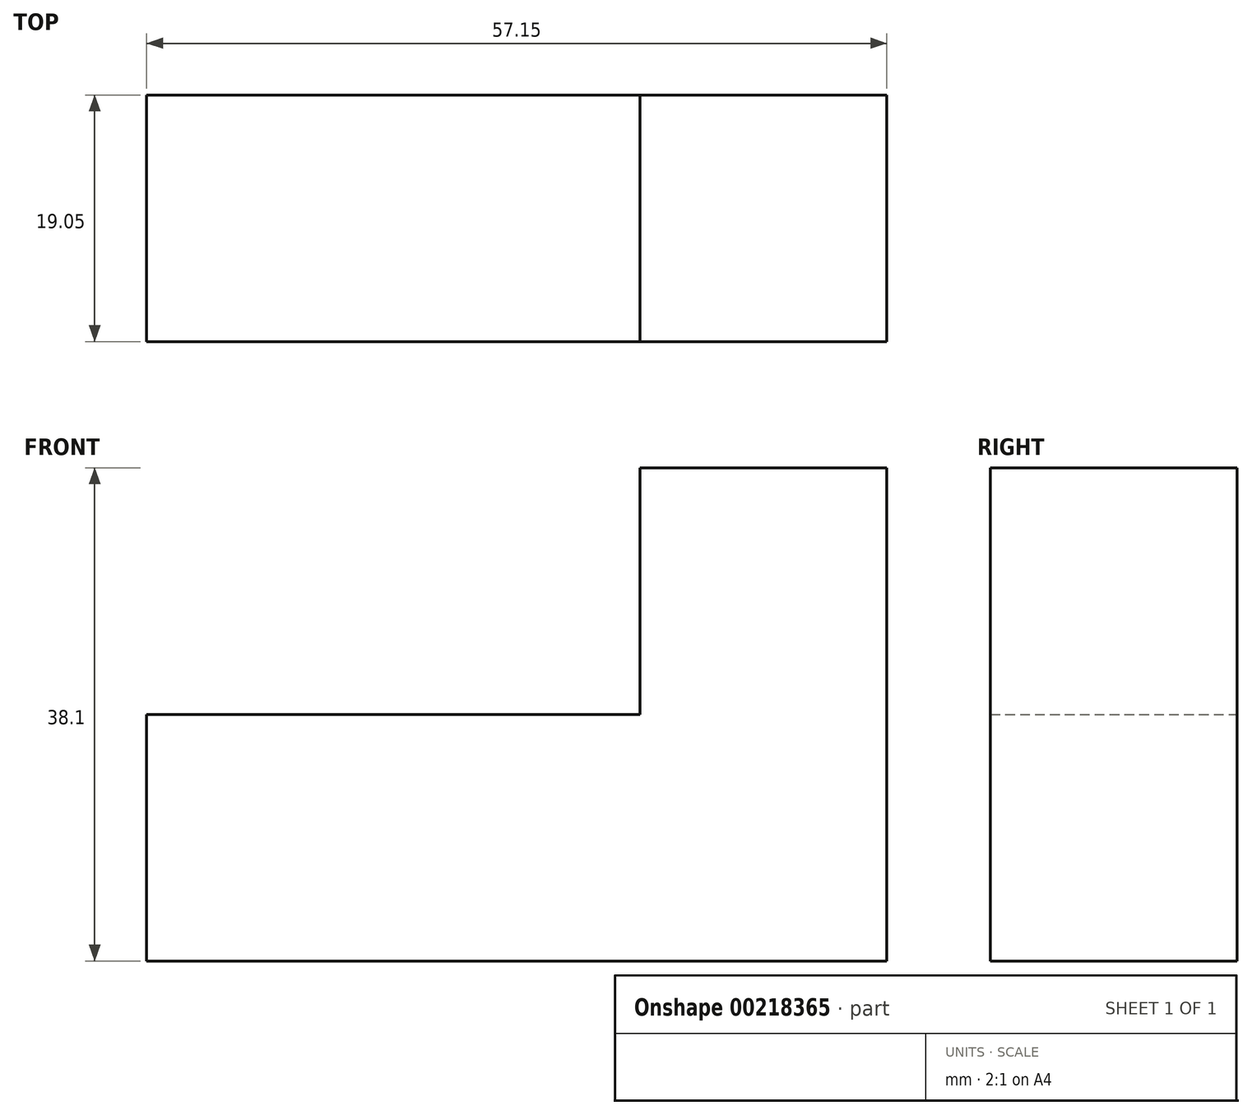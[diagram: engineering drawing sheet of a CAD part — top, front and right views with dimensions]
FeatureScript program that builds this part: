
annotation { "Feature Type Name" : "Feature", "Feature Type Description" : "" }
export const myFeature = defineFeature(function(context is Context, id is Id, definition is map)
    precondition{}
    {
        {
            var Q0;
            Q0=qCreatedBy(makeId("Front.planeOp"),FACE);
            var sketch = newSketch(context, id + "F0", { "sketchPlane" : qUnion([Q0])});
            skLineSegment(sketch, "E0.bottom", {"start": v(-57.15, 37.27) * mm, "end": v(-38.1, 37.27) * mm});
            skLineSegment(sketch, "E0.top", {"start": v(-57.15, 18.22) * mm, "end": v(-38.1, 18.22) * mm});
            skLineSegment(sketch, "E0.left", {"start": v(-57.15, 37.27) * mm, "end": v(-57.15, 18.22) * mm});
            skLineSegment(sketch, "E0.right", {"start": v(-38.1, 37.27) * mm, "end": v(-38.1, 18.22) * mm});
            skLineSegment(sketch, "E1.bottom", {"start": v(-38.1, 37.27) * mm, "end": v(-19.05, 37.27) * mm});
            skLineSegment(sketch, "E1.top", {"start": v(-38.1, 18.22) * mm, "end": v(-19.05, 18.22) * mm});
            skLineSegment(sketch, "E1.right", {"start": v(-19.05, 37.27) * mm, "end": v(-19.05, 18.22) * mm});
            skPoint(sketch, "E2.oppositeSnap0", {"position": v(-28.58, 18.22) * mm});
            skLineSegment(sketch, "E2.bottom", {"start": v(-19.05, 37.27) * mm, "end": v(0, 37.27) * mm});
            skLineSegment(sketch, "E2.top", {"start": v(-19.05, 18.22) * mm, "end": v(0, 18.22) * mm});
            skLineSegment(sketch, "E2.right", {"start": v(0, 37.27) * mm, "end": v(0, 18.22) * mm});
            skLineSegment(sketch, "E3.top", {"start": v(-19.05, 56.32) * mm, "end": v(0, 56.32) * mm});
            skLineSegment(sketch, "E3.left", {"start": v(-19.05, 37.27) * mm, "end": v(-19.05, 56.32) * mm});
            skLineSegment(sketch, "E3.right", {"start": v(0, 37.27) * mm, "end": v(0, 56.32) * mm});
            skSolve(sketch);
        }
        {
            var Q0;
            Q0=makeQuery(id+"F0.imprint","IMPRINT",FACE,{"disambiguationData":[TD([[makeQuery(id+"F0.imprint","IMPRINT",EDGE,{"derivedFrom":sQuery(id+"F0.wireOp",EDGE,"E0.bottom")}),-1.0]])]});
            var Q1;
            Q1=makeQuery(id+"F0.imprint","IMPRINT",FACE,{"disambiguationData":[TD([[makeQuery(id+"F0.imprint","IMPRINT",EDGE,{"derivedFrom":sQuery(id+"F0.wireOp",EDGE,"E1.bottom")}),-1.0]])]});
            var Q2;
            Q2=makeQuery(id+"F0.imprint","IMPRINT",FACE,{"disambiguationData":[TD([[makeQuery(id+"F0.imprint","IMPRINT",EDGE,{"derivedFrom":sQuery(id+"F0.wireOp",EDGE,"E2.top")}),1.0]])]});
            var Q3;
            Q3=makeQuery(id+"F0.imprint","IMPRINT",FACE,{"disambiguationData":[TD([[makeQuery(id+"F0.imprint","IMPRINT",EDGE,{"derivedFrom":sQuery(id+"F0.wireOp",EDGE,"E2.bottom")}),1.0]])]});
            extrude(context, id + "F1", {"entities" : qUnion([Q0, Q1, Q2, Q3]), "depth" : 19.05 * mm});
        }
    });
